# Revit family: RN 13002 Valvola di sicurezza
name_source: partatom
category: Rohrzubehör
units: mm (PartAtom-declared; Revit-internal decimal feet)

## family parameters
Arbeitsebenenbasiert = Nein
Beim Laden mit Abzugskörper schneiden = Nein
Bemaßung runder Anschluss = Durchmesser verwenden
Gemeinsam genutzt = Nein
Immer vertikal = Ja
Teiletyp = Ventil - Zerlegung in

## types (8) — shared parameters
1.010.00.2 Blattnummer der Richtlinie = 17
1.010.00.3 Ausgabedatum (Monat) der Richtlinie = 201601
1.010.00.4 Herstellername = R. Nussbaum AG
1.010.00.5 Revisionsdatum der Datei = 20190528
1.010.00.6 Webadresse des Herstellers = http://www.nussbaum.ch
1.100.00.3 Sortiernummer für Anzeigereihenfolge = 5
1.100.00.4 Produktbezeichnung = Sicherheitsarmaturen
1.960/3L.00.8 Link (URL) = https://www.nussbaum.ch
17.700.00.4 Armaturentyp = 12
17.700.00.7 Maximale Betriebstemperatur TB [°C] = 90
17.700.00.8 Maximaler Betriebsdruck (Arbeitsdruck) ps [1.0 · 105 Pa] = 10
Connector Visibility = Nein
EnclosingSpace Visibility = Nein
Hersteller = R. Nussbauzm AG
URL = https://www.nussbaum.ch

## per-type parameters (varying)
| type | 1.800.00.3 TGA-Nummer | 1.810.00.3 Hersteller-Bestellnummer | 1.810.00.4 DATANORM-Nummer | 1.810.00.6 GTIN-Nummer | 17.700.00.30 Produktbeschreibung | 17.700.00.5 Nennweite DN | CONNECTOR0_DIAMETER_dX_0r | CONNECTOR0_dX_00 | CONNECTOR0_dX_01 | CONNECTOR0_ref_dX | CONNECTOR1_DIAMETER_dZ_0r | CONNECTOR1_dZ_00 | CONNECTOR1_dZ_01 | CONNECTOR1_ref_dZ | Modell | R. Nussbaum AG 13002.21 de Visibility | R. Nussbaum AG 13002.22 de Visibility | R. Nussbaum AG 13002.23 de Visibility | R. Nussbaum AG 13002.31 de Visibility | R. Nussbaum AG 13002.32 de Visibility | R. Nussbaum AG 13002.33 de Visibility | R. Nussbaum AG 13002.42 de Visibility | R. Nussbaum AG 13002.43 de Visibility | Typenkommentare |
| DN 15 1 | 0050020000000000000000000000020070000000000000000100000000 | 13002.21 | 13002.21 | 7612945702630 | 13002.21, Sicherheitsventil, mit speziellen Druckeinstellungen, DN=15, R=½, Rp=¾ | 15 | 15 mm | 38 mm  [stored 0.124672 ft] | 23 mm | 38 mm  [stored 0.124672 ft] | 15 mm | 28 mm | 13 mm | 13 mm | 13002.21 | Ja | Nein | Nein | Nein | Nein | Nein | Nein | Nein | Valvola di sicurezzaDN 15 1 |
| DN 15 2 | 0050020000000000000000000000020070000000000000000200000000 | 13002.22 | 13002.22 | 7612945702647 | 13002.22, Sicherheitsventil, mit speziellen Druckeinstellungen, DN=15, R=½, Rp=¾ | 15 | 15 mm | 38 mm  [stored 0.124672 ft] | 23 mm | 38 mm  [stored 0.124672 ft] | 15 mm | 28 mm | 13 mm | 13 mm | 13002.22 | Nein | Ja | Nein | Nein | Nein | Nein | Nein | Nein | Valvola di sicurezzaDN 15 2 |
| DN 15 | 0050020000000000000000000000020070000000000000000300000000 | 13002.23 | 13002.23 | 7612945702654 | 13002.23, Sicherheitsventil, mit speziellen Druckeinstellungen, DN=15, R=½, Rp=¾ | 15 | 15 mm | 38 mm  [stored 0.124672 ft] | 23 mm | 38 mm  [stored 0.124672 ft] | 15 mm | 28 mm | 13 mm | 13 mm | 13002.23 | Nein | Nein | Ja | Nein | Nein | Nein | Nein | Nein | Valvola di sicurezzaDN 15 |
| DN 20 2 | 0050020000000000000000000000020070000000000000000400000000 | 13002.31 | 13002.31 | 7612945702661 | 13002.31, Sicherheitsventil, mit speziellen Druckeinstellungen, DN=20, R=¾, Rp=¾ | 20 | 20 mm | 40 mm | 25 mm  [stored 0.082021 ft] | 40 mm | 20 mm | 30 mm | 15 mm | 15 mm | 13002.31 | Nein | Nein | Nein | Ja | Nein | Nein | Nein | Nein | Valvola di sicurezzaDN 20 2 |
| DN 20 1 | 0050020000000000000000000000020070000000000000000500000000 | 13002.32 | 13002.32 | 7612945702685 | 13002.32, Sicherheitsventil, mit speziellen Druckeinstellungen, DN=20, R=¾, Rp=¾ | 20 | 20 mm | 40 mm | 25 mm  [stored 0.082021 ft] | 40 mm | 20 mm | 30 mm | 15 mm | 15 mm | 13002.32 | Nein | Nein | Nein | Nein | Ja | Nein | Nein | Nein | Valvola di sicurezzaDN 20 1 |
| DN 20 | 0050020000000000000000000000020070000000000000000600000000 | 13002.33 | 13002.33 | 7612945702739 | 13002.33, Sicherheitsventil, mit speziellen Druckeinstellungen, DN=20, R=¾, Rp=¾ | 20 | 20 mm | 40 mm | 25 mm  [stored 0.082021 ft] | 40 mm | 20 mm | 30 mm | 15 mm | 15 mm | 13002.33 | Nein | Nein | Nein | Nein | Nein | Ja | Nein | Nein | Valvola di sicurezzaDN 20 |
| DN 25 | 0050020000000000000000000000020070000000000000000700000000 | 13002.42 | 13002.42 | 7612945702746 | 13002.42, Sicherheitsventil, mit speziellen Druckeinstellungen, DN=25, R=1, Rp=1 | 25 | 25 mm  [stored 0.082021 ft] | 55 mm | 35 mm | 55 mm | 25 mm  [stored 0.082021 ft] | 32 mm | 15 mm | 15 mm | 13002.42 | Nein | Nein | Nein | Nein | Nein | Nein | Ja | Nein | Valvola di sicurezzaDN 25 |
| DN 25 1 | 0050020000000000000000000000020070000000000000000800000000 | 13002.43 | 13002.43 | 7612945702753 | 13002.43, Sicherheitsventil, mit speziellen Druckeinstellungen, DN=25, R=1, Rp=1 | 25 | 25 mm  [stored 0.082021 ft] | 55 mm | 35 mm | 55 mm | 25 mm  [stored 0.082021 ft] | 32 mm | 15 mm | 15 mm | 13002.43 | Nein | Nein | Nein | Nein | Nein | Nein | Nein | Ja | Valvola di sicurezzaDN 25 1 |

note: [stored X ft] marks values corroborated as IEEE doubles in the binary element streams (Revit-internal decimal feet)

## geometry (parser evidence)
native form markers: Sweep x1
no freeform markers — native parametric forms only
